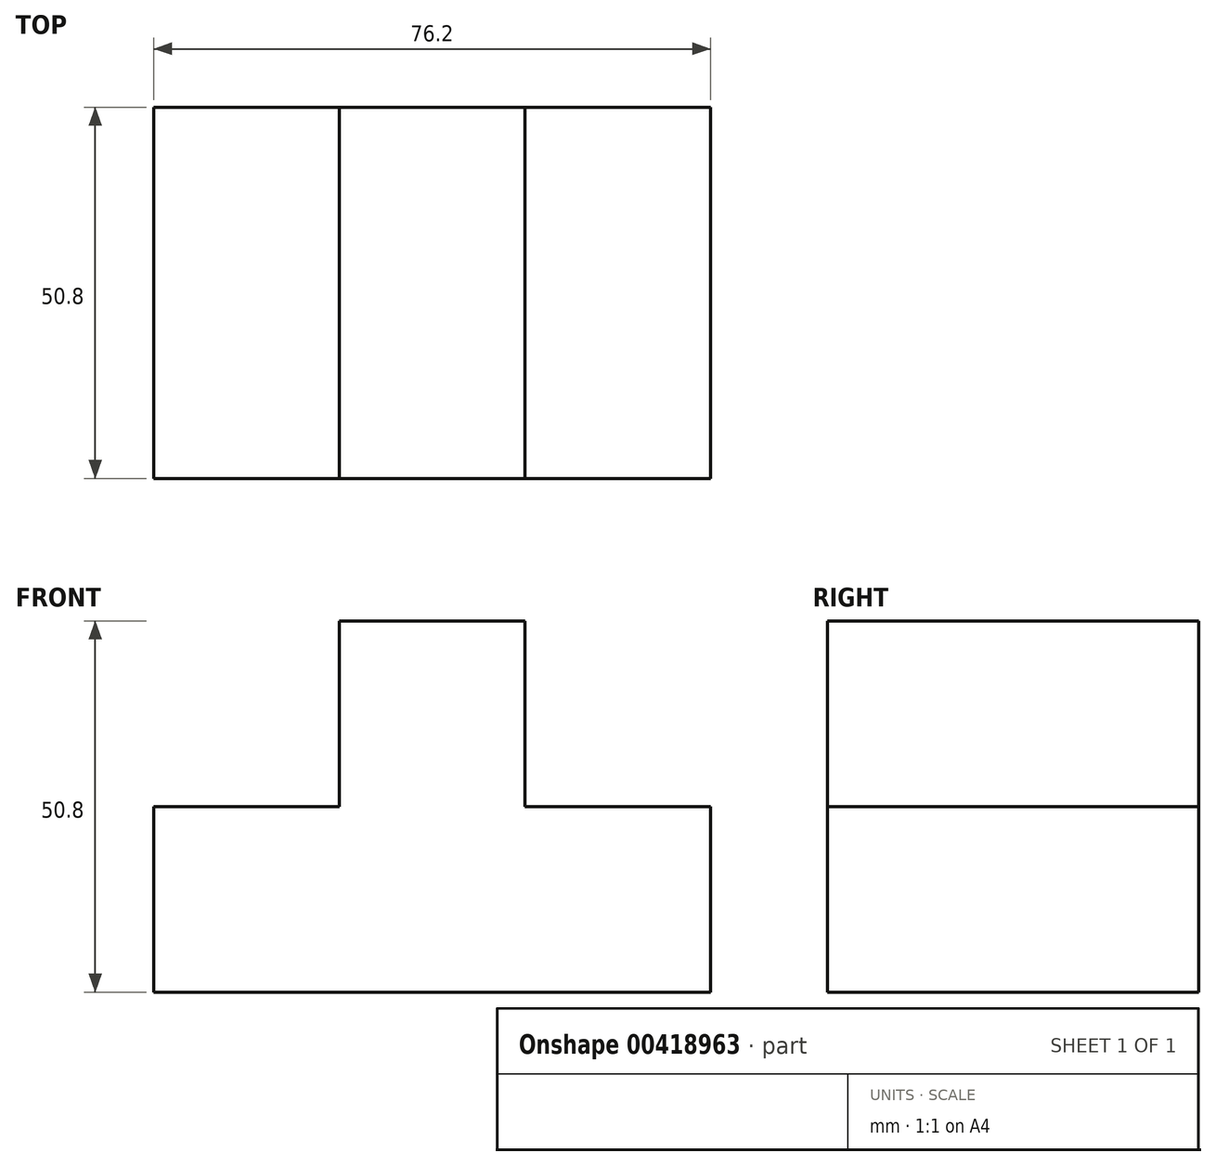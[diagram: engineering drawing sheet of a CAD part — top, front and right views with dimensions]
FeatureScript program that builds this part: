
annotation { "Feature Type Name" : "Feature", "Feature Type Description" : "" }
export const myFeature = defineFeature(function(context is Context, id is Id, definition is map)
    precondition{}
    {
        {
            var Q0;
            Q0=qCreatedBy(makeId("Front.planeOp"),FACE);
            var sketch = newSketch(context, id + "F0", { "sketchPlane" : qUnion([Q0])});
            skLineSegment(sketch, "E0", {"start": v(0, 0) * mm, "end": v(-76.2, 0) * mm});
            skLineSegment(sketch, "E1", {"start": v(-76.2, 25.4) * mm, "end": v(-76.2, 0) * mm});
            skLineSegment(sketch, "E2", {"start": v(-76.2, 25.4) * mm, "end": v(-50.8, 25.4) * mm});
            skLineSegment(sketch, "E3", {"start": v(-50.8, 25.4) * mm, "end": v(-50.8, 50.8) * mm});
            skLineSegment(sketch, "E4", {"start": v(-50.8, 50.8) * mm, "end": v(-25.4, 50.8) * mm});
            skLineSegment(sketch, "E5", {"start": v(-25.4, 50.8) * mm, "end": v(-25.4, 25.4) * mm});
            skLineSegment(sketch, "E6", {"start": v(-24.06, 25.4) * mm, "end": v(0, 25.4) * mm});
            skLineSegment(sketch, "E7", {"start": v(0, 25.4) * mm, "end": v(0, 0) * mm});
            skLineSegment(sketch, "E8", {"start": v(-24.06, 25.4) * mm, "end": v(-25.4, 25.4) * mm});
            skSolve(sketch);
        }
        {
            var Q0;
            Q0=makeQuery(id+"F0.imprint","IMPRINT",FACE,{"disambiguationData":[TD([[makeQuery(id+"F0.imprint","IMPRINT",EDGE,{"derivedFrom":sQuery(id+"F0.wireOp",EDGE,"E0")}),-1.0]])]});
            extrude(context, id + "F1", {"entities" : qUnion([Q0]), "depth" : 50.8 * mm});
        }
    });
